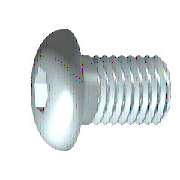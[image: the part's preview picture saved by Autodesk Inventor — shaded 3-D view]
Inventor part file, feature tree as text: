
AUTODESK INVENTOR PART (.ipt)
format: ipt  version: 2017 (Build 210142000, 142)  size: 199,168 bytes
history: native  units: mm (DEFAULTED — no unit token found)
features: sketch x2, extrude x1, plane x1, fillet x1
ambient origin geometry x7: Origin, YZ Plane, XY Plane, X Axis, Y Axis, Z Axis, Center Point
bodies: Solid1 (feature_tree), Body (feature_tree)
feature tree (5):
  extrude  "Slot"  Depth=1.8542mm
  plane  "Work Plane1"
  fillet  "Fillet2"  Radius=1.8542mm
  sketch  "Sketch1"  dims[d1=4.75976mm d2=1.59014mm d3=1.8542mm]
  sketch  "Sketch2"  dims[d4=1.1176mm d5=60.0deg d6=3.5052mm d7=3.5052mm d8=2.287693mm d9=6.6548mm d10=90.0deg d11=10.0mm d12=0.0mm d13=4.75976mm d14=0.0mm d15=0.486918mm d16=0.486918mm d17=1.6002mm d19=0.0mm d26=6.35mm d27=45.0deg d28=0.0mm d29=0.0mm d30=0.1mm]
